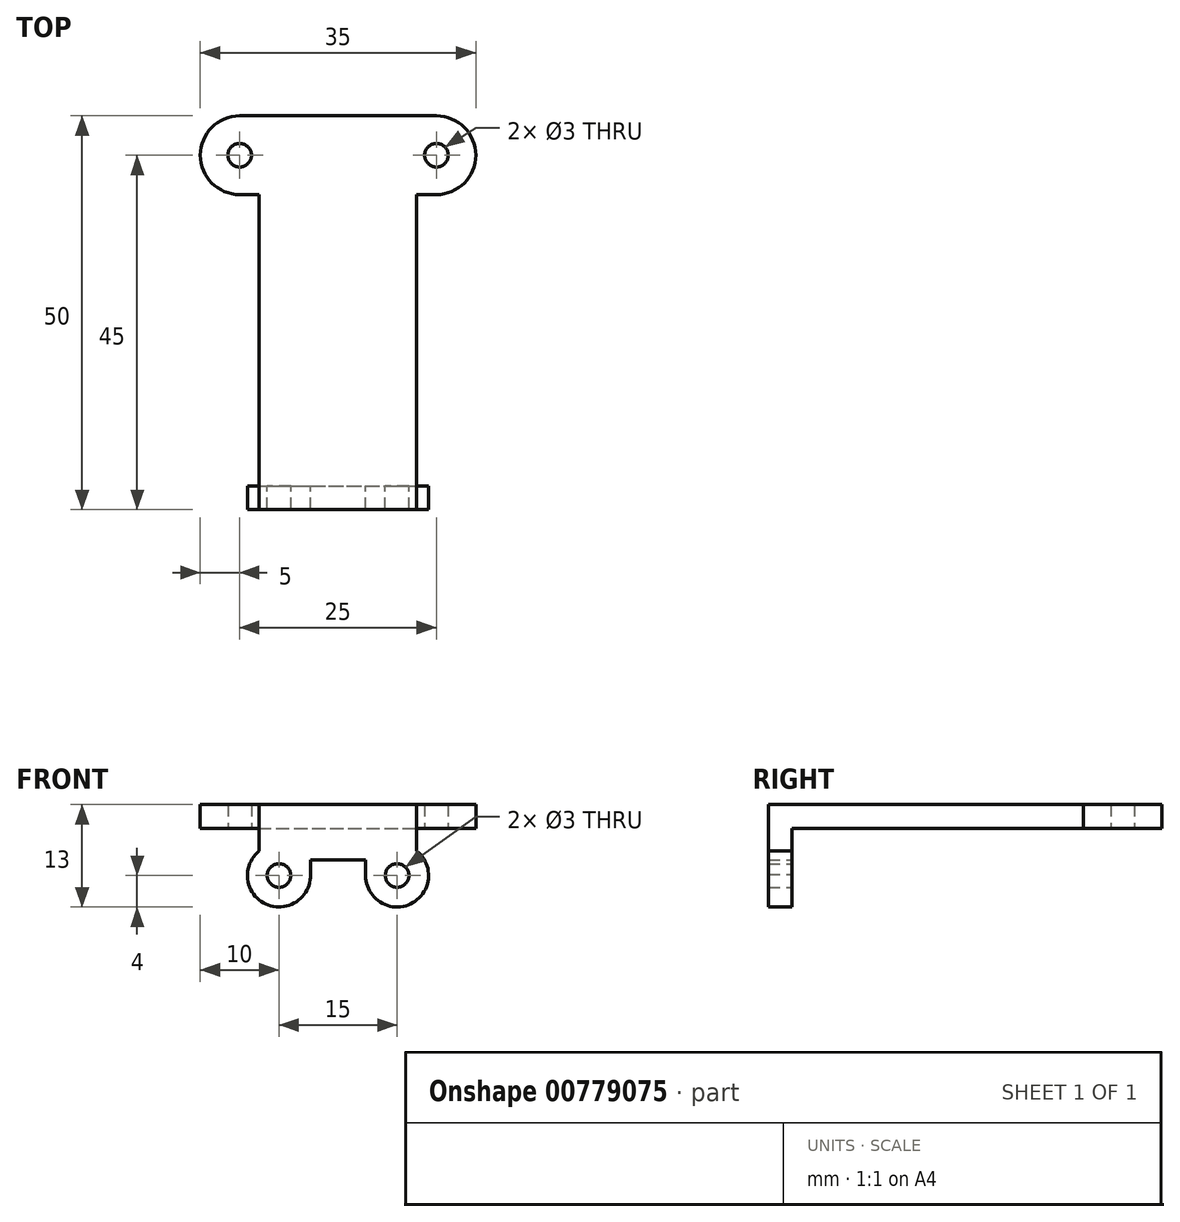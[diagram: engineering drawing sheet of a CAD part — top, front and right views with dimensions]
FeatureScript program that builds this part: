
annotation { "Feature Type Name" : "Feature", "Feature Type Description" : "" }
export const myFeature = defineFeature(function(context is Context, id is Id, definition is map)
    precondition{}
    {
        {
            var Q0;
            Q0=qCreatedBy(makeId("Front.planeOp"),FACE);
            var sketch = newSketch(context, id + "F0", { "sketchPlane" : qUnion([Q0])});
            skLineSegment(sketch, "E0.bottom", {"start": v(-10, 2) * mm, "end": v(10, 2) * mm});
            skLineSegment(sketch, "E0.top", {"start": v(-10, -2) * mm, "end": v(10, -2) * mm});
            skLineSegment(sketch, "E0.left", {"start": v(-10, 2) * mm, "end": v(-10, -2) * mm});
            skLineSegment(sketch, "E0.right", {"start": v(10, 2) * mm, "end": v(10, -2) * mm});
            skPoint(sketch, "E0.middle", {"position": v(0, 0) * mm});
            skCircle(sketch, "E1", {"center": v(-7.5, -4) * mm, "radius": 4 * mm});
            skCircle(sketch, "E2", {"center": v(7.5, -4) * mm, "radius": 4 * mm});
            skCircle(sketch, "E3", {"center": v(-7.5, -4) * mm, "radius": 1.5 * mm});
            skCircle(sketch, "E4", {"center": v(7.5, -4) * mm, "radius": 1.5 * mm});
            skLineSegment(sketch, "E5", {"start": v(-3.5, -4.11) * mm, "end": v(-3.5, -2) * mm});
            skLineSegment(sketch, "E6", {"start": v(3.5, -4) * mm, "end": v(3.5, -2) * mm});
            skSolve(sketch);
        }
        {
            var Q0;
            Q0 = qSketchRegion(id + "F0", true);
            extrude(context, id + "F1", {"entities" : qUnion([Q0]), "depth" : 3 * mm, "offsetDistance" : 25 * mm});
        }
        {
            var Q0;
            Q0=makeQuery(id+"F1.opExtrude","SWEPT_FACE",FACE,{"disambiguationData":[OSD([sQuery(id+"F0.wireOp",EDGE,"E0.bottom")])]});
            var sketch = newSketch(context, id + "F2", { "sketchPlane" : qUnion([Q0])});
            skLineSegment(sketch, "E7.bottom", {"start": v(-10, -3) * mm, "end": v(10, -3) * mm});
            skLineSegment(sketch, "E7.top", {"start": v(-10, 47) * mm, "end": v(10, 47) * mm});
            skLineSegment(sketch, "E7.left", {"start": v(-10, -3) * mm, "end": v(-10, 47) * mm});
            skLineSegment(sketch, "E7.right", {"start": v(10, -3) * mm, "end": v(10, 47) * mm});
            skCircle(sketch, "E8", {"center": v(-12.5, 42) * mm, "radius": 1.5 * mm});
            skCircle(sketch, "E9", {"center": v(12.5, 42) * mm, "radius": 1.5 * mm});
            skLineSegment(sketch, "E10.bottom", {"start": v(-12.5, 47) * mm, "end": v(12.5, 47) * mm});
            skLineSegment(sketch, "E10.top", {"start": v(-12.5, 37) * mm, "end": v(12.5, 37) * mm});
            skLineSegment(sketch, "E10.left", {"start": v(-17.5, 42) * mm, "end": v(-17.5, 42) * mm});
            skLineSegment(sketch, "E10.right", {"start": v(17.5, 42) * mm, "end": v(17.5, 42) * mm});
            skPoint(sketch, "E11.visualSharp", {"position": v(17.5, 37) * mm});
            skArc(sketch, "E11.filletArc", {"start": v(12.5, 37) * mm, "mid": v(16.04, 38.46) * mm, "end": v(17.5, 42) * mm});
            skPoint(sketch, "E12.visualSharp", {"position": v(17.5, 47) * mm});
            skArc(sketch, "E12.filletArc", {"start": v(17.5, 42) * mm, "mid": v(16.04, 45.54) * mm, "end": v(12.5, 47) * mm});
            skPoint(sketch, "E13.visualSharp", {"position": v(-17.5, 47) * mm});
            skArc(sketch, "E13.filletArc", {"start": v(-12.5, 47) * mm, "mid": v(-16.04, 45.54) * mm, "end": v(-17.5, 42) * mm});
            skPoint(sketch, "E14.visualSharp", {"position": v(-17.5, 37) * mm});
            skArc(sketch, "E14.filletArc", {"start": v(-17.5, 42) * mm, "mid": v(-16.04, 38.46) * mm, "end": v(-12.5, 37) * mm});
            skSolve(sketch);
        }
        {
            var Q0;
            Q0 = qSketchRegion(id + "F2", true);
            extrude(context, id + "F3", {"entities" : qUnion([Q0]), "operationType" : NewBodyOperationType.ADD, "depth" : 3 * mm, "offsetDistance" : 25 * mm});
        }
    });
